FCSTD DOCUMENT
Label: PR_029_túlhatározott
objects: Sketcher::SketchObject×1
note: 1 computed .brp shape members not serialized (recipe doc carries the construction recipe); baked Part::Feature solids carry a one-line shape summary decoded from their .brp

FEATURE [Sketcher::SketchObject] Sketch
  sketch-geometry (6):
    g0: LineSegment StartX=30 StartY=-954.92 StartZ=0 EndX=211 EndY=-954.92 EndZ=0
    g1: LineSegment [constr] StartX=0 StartY=-1054.92 StartZ=0 EndX=250 EndY=-1054.92 EndZ=0
    g2: LineSegment [constr] StartX=250 StartY=-1054.92 StartZ=0 EndX=250 EndY=-919.283 EndZ=0
    g3: ArcOfCircle CenterX=30 CenterY=-984.92 CenterZ=0 NormalX=0 NormalY=0 NormalZ=1 Radius=30 StartAngle=1.5708 EndAngle=4.09435
    g4: ArcOfCircle CenterX=211 CenterY=-993.92 CenterZ=0 NormalX=0 NormalY=0 NormalZ=1 Radius=39 StartAngle=5.14511 EndAngle=7.85398
    g5: ArcOfCircle CenterX=137.196 CenterY=-834.142 CenterZ=0 NormalX=0 NormalY=0 NormalZ=1 Radius=215 StartAngle=4.09435 EndAngle=5.14511
  constraints (18):
    c: Horizontal(g0)
    c: DistanceY(g0) = -954.92
    c: Horizontal(g1)
    c: DistanceY(g0,g1) = -100
    c: DistanceX(g1) = 0
    c: Distance(g1) = 250
    c: Coincident(g2,g1)
    c: Vertical(g2)
    c: Radius(g5) = 215
    c: Radius(g3) = 30
    c: Tangent(g3,g0)
    c: Radius(g4) = 39
    c: Tangent(g5,g4)
    c: Tangent(g3,g5)
    c: Tangent(g0,g4)
    c: Tangent(g3,g-2)
    c: Tangent(g4,g2)
    c: DistanceY(g2) = -919.283
